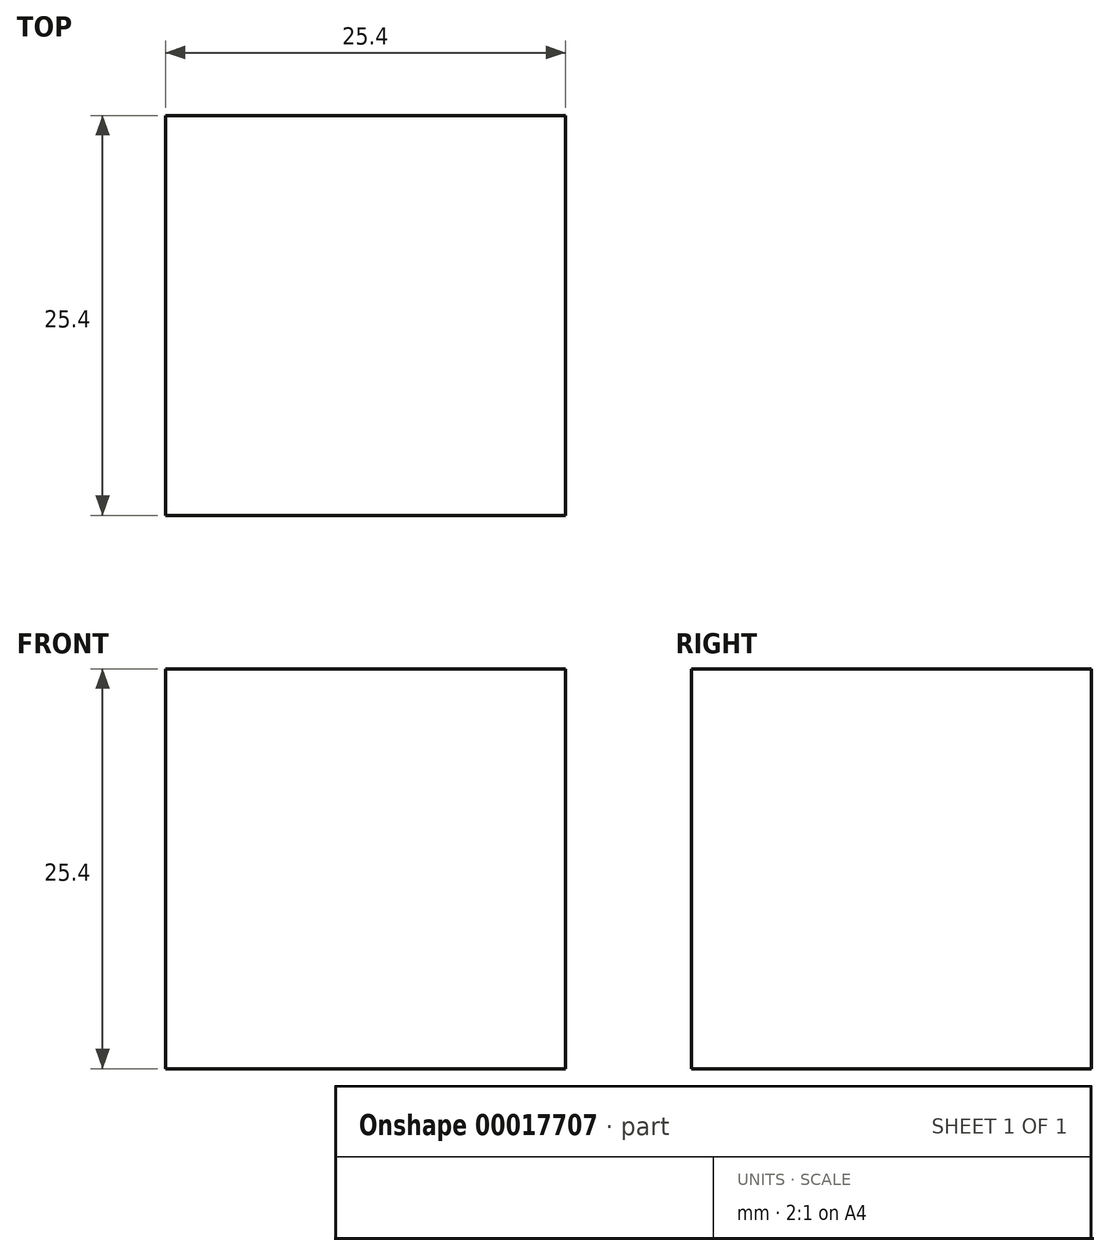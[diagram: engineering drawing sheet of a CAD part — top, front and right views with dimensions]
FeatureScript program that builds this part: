
annotation { "Feature Type Name" : "Feature", "Feature Type Description" : "" }
export const myFeature = defineFeature(function(context is Context, id is Id, definition is map)
    precondition{}
    {
        {
            var Q0;
            Q0=qCreatedBy(makeId("Top.planeOp"),FACE);
            var sketch = newSketch(context, id + "F0", { "sketchPlane" : qUnion([Q0])});
            skLineSegment(sketch, "E0.bottom", {"start": v(0, 0) * mm, "end": v(25.4, 0) * mm});
            skLineSegment(sketch, "E0.top", {"start": v(0, 25.4) * mm, "end": v(25.4, 25.4) * mm});
            skLineSegment(sketch, "E0.left", {"start": v(0, 0) * mm, "end": v(0, 25.4) * mm});
            skLineSegment(sketch, "E0.right", {"start": v(25.4, 0) * mm, "end": v(25.4, 25.4) * mm});
            skSolve(sketch);
        }
        {
            var Q0;
            Q0=makeQuery(id+"F0.imprint","IMPRINT",FACE,{"disambiguationData":[TD([[makeQuery(id+"F0.imprint","IMPRINT",EDGE,{"derivedFrom":sQuery(id+"F0.wireOp",EDGE,"E0.bottom")}),1.0]])]});
            extrude(context, id + "F1", {"entities" : qUnion([Q0]), "depth" : 25.4 * mm});
        }
    });
